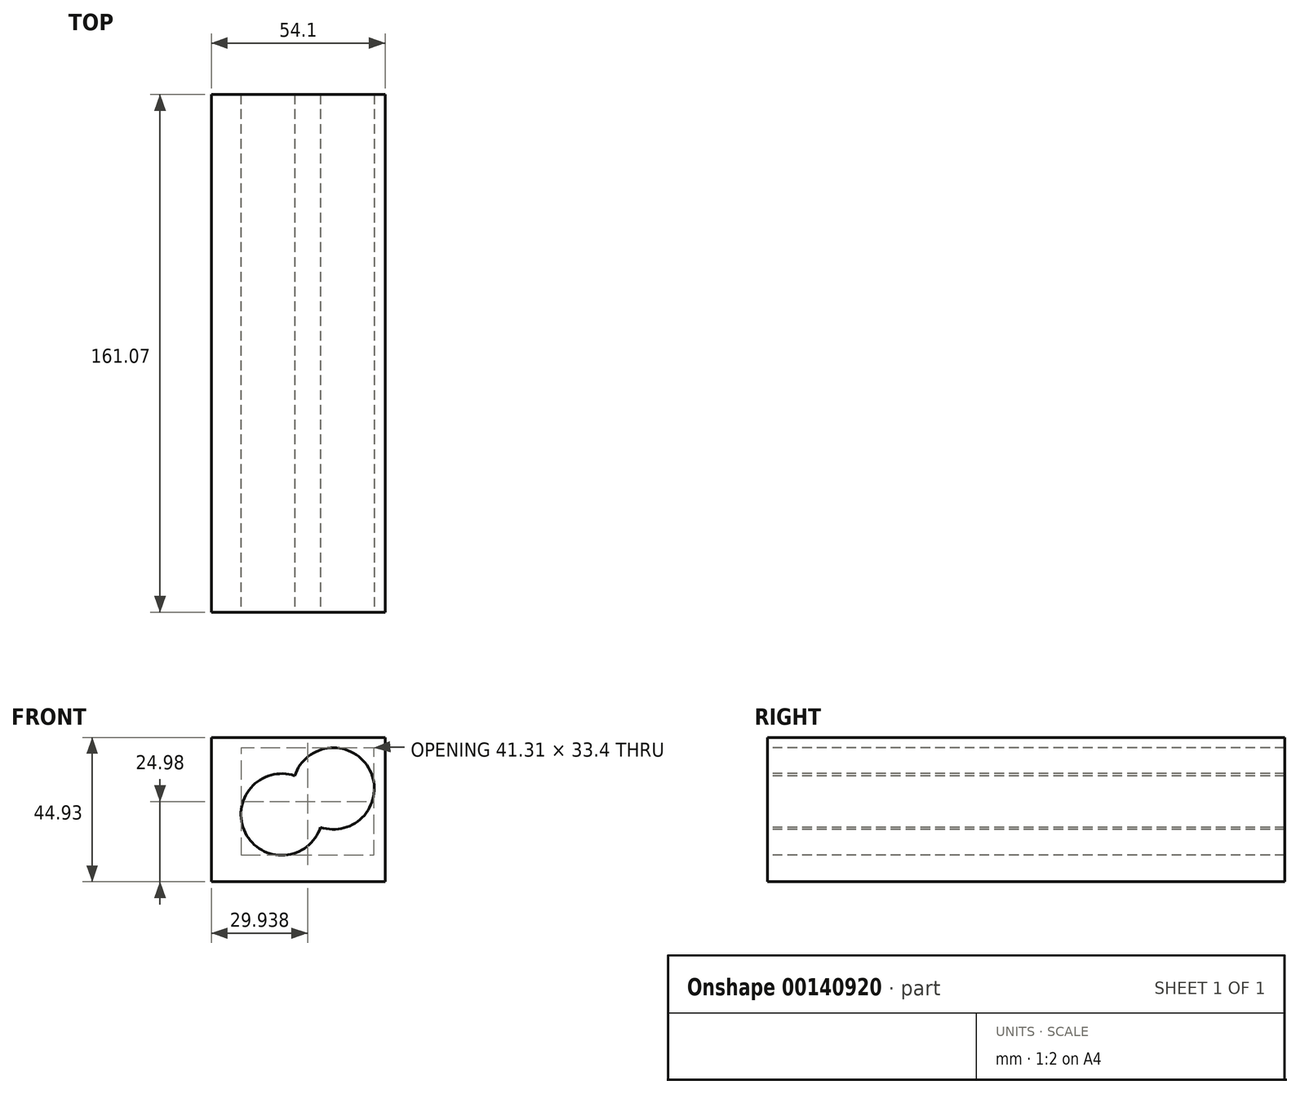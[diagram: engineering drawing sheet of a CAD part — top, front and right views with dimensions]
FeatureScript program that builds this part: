
annotation { "Feature Type Name" : "Feature", "Feature Type Description" : "" }
export const myFeature = defineFeature(function(context is Context, id is Id, definition is map)
    precondition{}
    {
        {
            var Q0;
            Q0=qCreatedBy(makeId("Front.planeOp"),FACE);
            var sketch = newSketch(context, id + "F0", { "sketchPlane" : qUnion([Q0])});
            skLineSegment(sketch, "E0.bottom", {"start": v(-15.25, 60.98) * mm, "end": v(-69.35, 60.98) * mm});
            skLineSegment(sketch, "E0.top", {"start": v(-15.25, 16.05) * mm, "end": v(-69.35, 16.05) * mm});
            skLineSegment(sketch, "E0.left", {"start": v(-15.25, 60.98) * mm, "end": v(-15.25, 16.05) * mm});
            skLineSegment(sketch, "E0.right", {"start": v(-69.35, 60.98) * mm, "end": v(-69.35, 16.05) * mm});
            skSolve(sketch);
        }
        {
            var Q0;
            Q0=makeQuery(id+"F0.imprint","IMPRINT",FACE,{"disambiguationData":[TD([[makeQuery(id+"F0.imprint","IMPRINT",EDGE,{"derivedFrom":sQuery(id+"F0.wireOp",EDGE,"E0.bottom")}),1.0]])]});
            extrude(context, id + "F1", {"entities" : qUnion([Q0]), "depth" : 161.07 * mm});
        }
        {
            var Q0;
            Q0=makeQuery(id+"F1.opExtrude","CAP_FACE",FACE,{"disambiguationData":[OSD([sQuery(id+"F0.wireOp",EDGE,"E0.bottom"),sQuery(id+"F0.wireOp",EDGE,"E0.top"),sQuery(id+"F0.wireOp",EDGE,"E0.left"),sQuery(id+"F0.wireOp",EDGE,"E0.right")])],"isStart":false});
            var sketch = newSketch(context, id + "F2", { "sketchPlane" : qUnion([Q0])});
            skCircle(sketch, "E1", {"center": v(-47.47, 37) * mm, "radius": 9.87 * mm});
            skSolve(sketch);
        }
        {
            var Q0;
            Q0=makeQuery(id+"F2.imprint","IMPRINT",FACE,{"disambiguationData":[TD([[makeQuery(id+"F2.imprint","IMPRINT",EDGE,{"derivedFrom":sQuery(id+"F2.wireOp",EDGE,"E1")}),-1.0]])]});
            var sketch = newSketch(context, id + "F3", { "sketchPlane" : qUnion([Q0])});
            skCircle(sketch, "E2", {"center": v(-31.36, 45.06) * mm, "radius": 11.22 * mm});
            skSolve(sketch);
        }
        {
            var Q0;
            Q0=sQuery(id+"F2.wireOp",VERTEX,"E1.center");
            var Q1;
            Q1=makeQuery(id+"F1.opExtrude","SWEPT_BODY",BODY,{"disambiguationData":[OSD([sQuery(id+"F0.wireOp",EDGE,"E0.bottom"),sQuery(id+"F0.wireOp",EDGE,"E0.top"),sQuery(id+"F0.wireOp",EDGE,"E0.left"),sQuery(id+"F0.wireOp",EDGE,"E0.right")])]});
            hole(context, id + "F4", {"style" : HoleStyle.SIMPLE, "endStyle" : HoleEndStyle.THROUGH, "holeDiameter" : 25.4 * mm, "locations" : qUnion([Q0]), "scope" : qUnion([Q1]), "isTappedThrough" : true});
        }
        {
            var Q0;
            Q0=sQuery(id+"F3.wireOp",VERTEX,"E2.center");
            var Q1;
            Q1=makeQuery(id+"F1.opExtrude","SWEPT_BODY",BODY,{"disambiguationData":[OSD([sQuery(id+"F0.wireOp",EDGE,"E0.bottom"),sQuery(id+"F0.wireOp",EDGE,"E0.top"),sQuery(id+"F0.wireOp",EDGE,"E0.left"),sQuery(id+"F0.wireOp",EDGE,"E0.right")])]});
            hole(context, id + "F5", {"style" : HoleStyle.SIMPLE, "endStyle" : HoleEndStyle.THROUGH, "holeDiameter" : 25.4 * mm, "locations" : qUnion([Q0]), "scope" : qUnion([Q1]), "isTappedThrough" : true});
        }
    });
